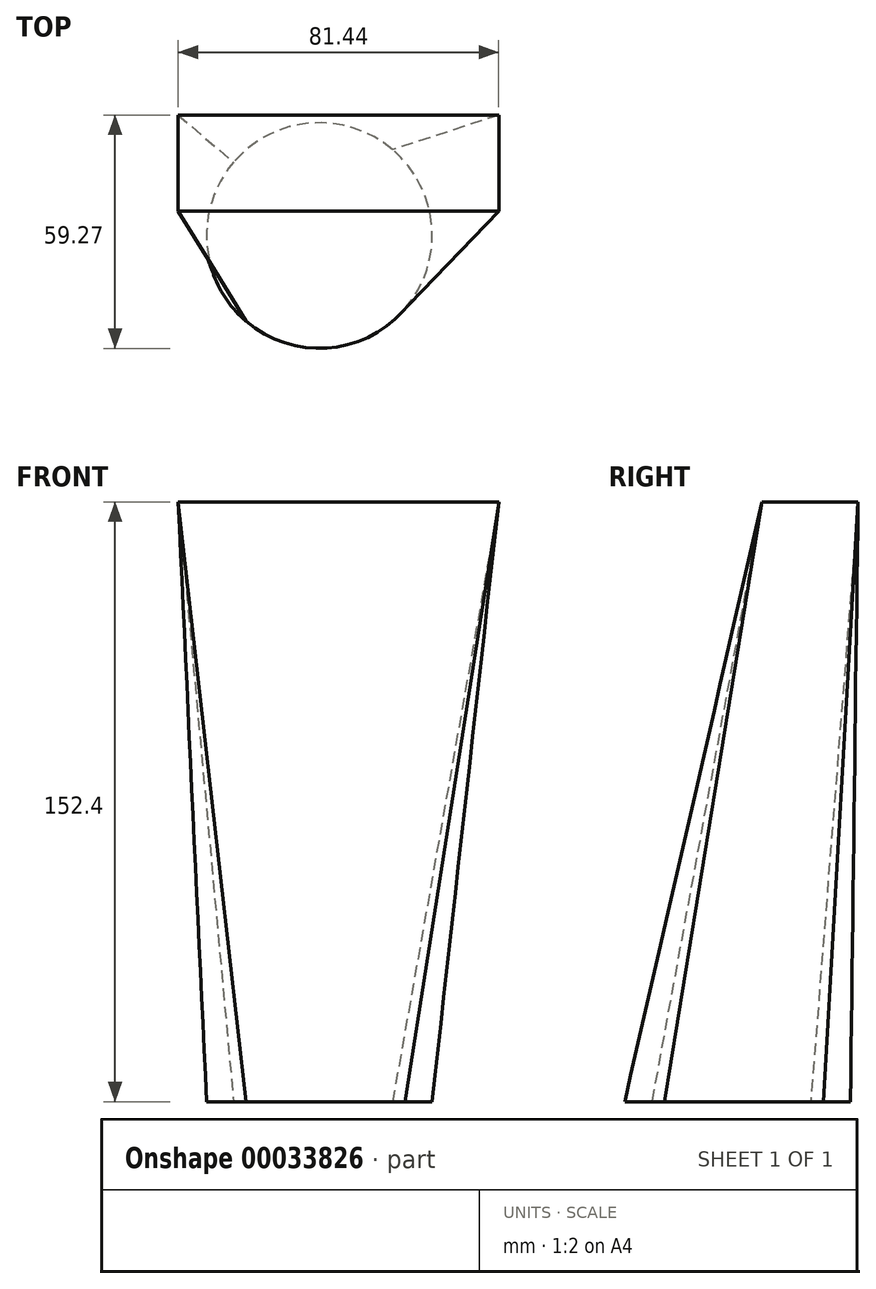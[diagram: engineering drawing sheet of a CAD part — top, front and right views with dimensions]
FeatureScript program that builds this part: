
annotation { "Feature Type Name" : "Feature", "Feature Type Description" : "" }
export const myFeature = defineFeature(function(context is Context, id is Id, definition is map)
    precondition{}
    {
        {
            var Q0;
            Q0=qCreatedBy(makeId("Top.planeOp"),FACE);
            var sketch = newSketch(context, id + "F0", { "sketchPlane" : qUnion([Q0])});
            skCircle(sketch, "E0", {"center": v(0, 0) * mm, "radius": 28.66 * mm});
            skSolve(sketch);
        }
        {
            var Q0;
            Q0=qCreatedBy(makeId("Top.planeOp"),FACE);
            cPlane(context, id + "F1", {"entities" : qUnion([Q0]), "cplaneType" : CPlaneType.OFFSET, "offset" : 152.4 * mm, "width" : 152.4 * mm, "height" : 152.4 * mm});
        }
        {
            var Q0;
            Q0=qCreatedBy(id+"F1.planeOp",FACE);
            var sketch = newSketch(context, id + "F2", { "sketchPlane" : qUnion([Q0])});
            skLineSegment(sketch, "E1.bottom", {"start": v(-35.86, 30.61) * mm, "end": v(45.58, 30.61) * mm});
            skLineSegment(sketch, "E1.top", {"start": v(-35.86, 6.2) * mm, "end": v(45.58, 6.2) * mm});
            skLineSegment(sketch, "E1.left", {"start": v(-35.86, 30.61) * mm, "end": v(-35.86, 6.2) * mm});
            skLineSegment(sketch, "E1.right", {"start": v(45.58, 30.61) * mm, "end": v(45.58, 6.2) * mm});
            skSolve(sketch);
        }
        {
            var Q0;
            Q0=makeQuery(id+"F2.imprint","IMPRINT",FACE,{"disambiguationData":[TD([[makeQuery(id+"F2.imprint","IMPRINT",EDGE,{"derivedFrom":sQuery(id+"F2.wireOp",EDGE,"E1.bottom")}),-1.0]])]});
            var Q1;
            Q1=makeQuery(id+"F0.imprint","IMPRINT",FACE,{"disambiguationData":[TD([[makeQuery(id+"F0.imprint","IMPRINT",EDGE,{"derivedFrom":sQuery(id+"F0.wireOp",EDGE,"E0")}),1.0]])]});
            loft(context, id + "F3", {"sheetProfilesArray" : [{ "sheetProfileEntities" : qUnion([Q0]) }, { "sheetProfileEntities" : qUnion([Q1]) }]});
        }
    });
